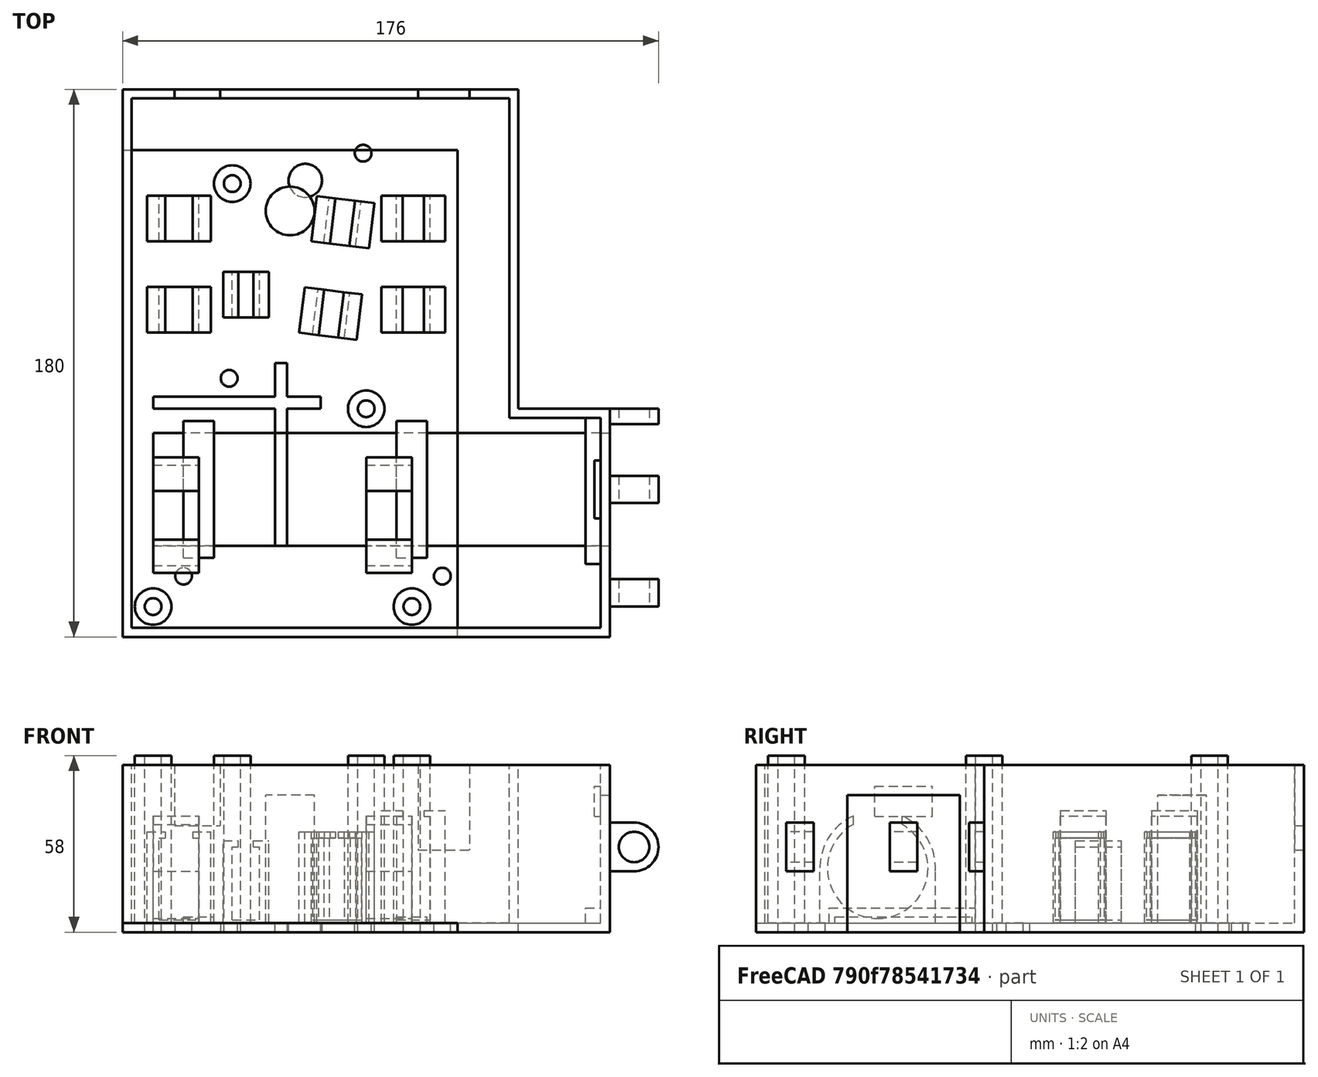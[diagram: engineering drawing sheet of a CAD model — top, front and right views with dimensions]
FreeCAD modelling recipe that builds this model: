
FCSTD DOCUMENT  (FreeCAD 0.16R6707 (Git))
Label: Akku_Peripherie
License: All rights reserved
LicenseURL: http://en.wikipedia.org/wiki/All_rights_reserved
objects: Part::Box×37, Part::Cylinder×23, Part::Cut×20, Part::MultiFuse×18, App::DocumentObjectGroup×4, Spreadsheet::Sheet×1, Mesh::Feature×1
note: 98 computed .brp shape members not serialized (recipe doc carries the construction recipe); baked Part::Feature solids carry a one-line shape summary decoded from their .brp

FEATURE [Part::Box] Box  label="Grundplatte"
  Height = 3
  Length = 110
  Width = 160
FEATURE [Part::Cylinder] Cylinder003  label="PowerCore"
  Angle = 360
  Height = 108
  Placement = pos=(0,40,21) rot=(0,1,0;1.5708rad)
  Radius = 16.5
FEATURE [Part::Cylinder] Cylinder004  label="PowerCore001"
  Angle = 360
  Height = 15
  Placement = pos=(10,40,21) rot=(0,1,0;1.5708rad)
  Radius = 19
FEATURE [Part::Cylinder] Cylinder005  label="PowerCore002"
  Angle = 360
  Height = 15
  Placement = pos=(80,40,21) rot=(0,1,0;1.5708rad)
  Radius = 19
FEATURE [Part::MultiFuse] Fusion
  Shapes = -> [Cylinder004,Cylinder005]
FEATURE [Part::Cut] Cut
  Base = -> Fusion
  Tool = -> Cylinder003
FEATURE [Part::Box] Box001  label="Würfel001"
  Height = 10
  Length = 108
  Placement = pos=(0,32,33) rot=(0,0,1;0rad)
  Width = 16
FEATURE [Part::Cut] Cut001  label="Anker Powerbank"
  Base = -> Cut
  Tool = -> Box001
FEATURE [Part::Cylinder] Cylinder  label="Hull Corner 1"
  Angle = 360
  Height = 55
  Placement = pos=(10,10,3) rot=(0,0,1;0rad)
  Radius = 6
FEATURE [Part::Cylinder] Cylinder006  label="Core Corner 4"
  Angle = 360
  Height = 70
  Placement = pos=(95,10,-3) rot=(0,0,1;0rad)
  Radius = 2.75
FEATURE [App::DocumentObjectGroup] Gruppe001  label="Devices"
FEATURE [Part::Box] Box002  label="DVB-T"
  Height = 27
  Length = 84
  Placement = pos=(25,80,4) rot=(0,0,1;1.5708rad)
  Width = 13
FEATURE [Part::Box] Box003  label="GPS"
  Height = 24
  Length = 52
  Placement = pos=(45,80,4) rot=(0,0,1;1.5708rad)
  Width = 9
FEATURE [Part::Cylinder] Cylinder007  label="Core Corner 2"
  Angle = 360
  Height = 70
  Placement = pos=(36,149,-3) rot=(0,0,1;0rad)
  Radius = 2.75
FEATURE [Part::Cylinder] Cylinder008  label="Hull Corner 2"
  Angle = 360
  Height = 55
  Placement = pos=(36,149,3) rot=(0,0,1;0rad)
  Radius = 6
FEATURE [Part::Cylinder] Cylinder009  label="Hull Corner 4"
  Angle = 360
  Height = 55
  Placement = pos=(95,10,3) rot=(0,0,1;0rad)
  Radius = 6
FEATURE [Part::Cylinder] Cylinder010  label="Core Corner 1"
  Angle = 360
  Height = 70
  Placement = pos=(10,10,-3) rot=(0,0,1;0rad)
  Radius = 2.75
FEATURE [Part::Box] Box004  label="Würfel002"
  Height = 33
  Length = 21
  Placement = pos=(8,100,0) rot=(0,0,1;0rad)
  Width = 15
FEATURE [Part::Box] Box005  label="Würfel003"
  Height = 33
  Length = 21
  Placement = pos=(8,130,0) rot=(0,0,1;0rad)
  Width = 15
FEATURE [Part::Box] Box006  label="Halterung"
  Height = 10
  Length = 9
  Placement = pos=(14,95,30) rot=(0,0,1;0rad)
  Width = 60
FEATURE [Part::MultiFuse] Fusion001
  Shapes = -> [Box005,Box004]
FEATURE [Part::Cut] Cut002
  Base = -> Fusion001
  Tool = -> Box006
FEATURE [Part::Cut] Cut003  label="DVB-T Halterung"
  Base = -> Cut002
  Tool = -> Box002
FEATURE [Part::Box] Box007  label="Würfel004"
  Height = 30
  Length = 15
  Placement = pos=(33,105,0) rot=(0,0,1;0rad)
  Width = 15
FEATURE [Part::Box] Box008  label="GPS001"
  Height = 24
  Length = 52
  Placement = pos=(43,80,10) rot=(0,0,1;1.5708rad)
  Width = 5
FEATURE [Part::MultiFuse] Fusion002
  Shapes = -> [Box008,Box003]
FEATURE [Part::Cut] Cut004  label="GPS Halterung"
  Base = -> Box007
  Tool = -> Fusion002
FEATURE [Part::Box] Box009  label="Würfel"
  Height = 55
  Length = 160
  Width = 180
FEATURE [Part::Box] Box010  label="Alfa"
  Height = 34
  Length = 11
  Placement = pos=(90,80,4) rot=(0,0,1;0rad)
  Width = 87
FEATURE [Part::Box] Box011  label="Würfel005"
  Height = 40
  Length = 21
  Placement = pos=(85,130,0) rot=(0,0,1;0rad)
  Width = 15
FEATURE [Part::Box] Box012  label="Würfel006"
  Height = 40
  Length = 21
  Placement = pos=(85,100,0) rot=(0,0,1;0rad)
  Width = 15
FEATURE [Part::MultiFuse] Fusion003
  Shapes = -> [Box012,Box011]
FEATURE [Part::Box] Box013  label="Alfa001"
  Height = 34
  Length = 7
  Placement = pos=(92,80,10) rot=(0,0,1;0rad)
  Width = 87
FEATURE [Part::MultiFuse] Fusion004
  Shapes = -> [Box013,Box010]
FEATURE [Part::Cut] Cut005  label="Alfa Halterung"
  Base = -> Fusion003
  Tool = -> Fusion004
FEATURE [Part::Cylinder] Cylinder012  label="Hull Corner 3"
  Angle = 360
  Height = 55
  Placement = pos=(80,75,3) rot=(0,0,1;0rad)
  Radius = 6
FEATURE [Part::Cylinder] Cylinder013  label="Core Corner 3"
  Angle = 360
  Height = 70
  Placement = pos=(80,75,-3) rot=(0,0,1;0rad)
  Radius = 2.75
FEATURE [Part::Box] Box014  label="Würfel007"
  Height = 55
  Length = 30
  Placement = pos=(130,75,0) rot=(0,0,1;0rad)
  Width = 105
FEATURE [Part::Box] Box015  label="Würfel008"
  Height = 55
  Length = 124
  Placement = pos=(3,3,3) rot=(0,0,1;0rad)
  Width = 174
FEATURE [Part::Box] Box016  label="Würfel009"
  Height = 55
  Length = 30
  Placement = pos=(127,3,3) rot=(0,0,1;0rad)
  Width = 69
FEATURE [Part::Cylinder] Cylinder014  label="Zylinder"
  Angle = 360
  Height = 10
  Placement = pos=(20,20,-3) rot=(0,0,1;0rad)
  Radius = 2.75
FEATURE [Part::Cylinder] Cylinder015  label="Zylinder001"
  Angle = 360
  Height = 10
  Placement = pos=(105,20,-3) rot=(0,0,1;0rad)
  Radius = 2.75
FEATURE [Part::Cylinder] Cylinder016  label="Zylinder002"
  Angle = 360
  Height = 10
  Placement = pos=(79,159,-3) rot=(0,0,1;0rad)
  Radius = 2.75
FEATURE [Part::Cylinder] Cylinder017  label="Zylinder003"
  Angle = 360
  Height = 10
  Placement = pos=(35,85,-3) rot=(0,0,1;0rad)
  Radius = 2.75
FEATURE [Part::Cylinder] Cylinder018  label="Zylinder004"
  Angle = 360
  Height = 10
  Placement = pos=(60,150,-3) rot=(0,0,1;0rad)
  Radius = 5.5
FEATURE [Part::MultiFuse] Fusion008
  Shapes = -> [Cylinder014,Cylinder015,Cylinder016,Cylinder017,Cylinder018]
FEATURE [Part::Box] Box017  label="Würfel010"
  Height = 28
  Length = 17
  Placement = pos=(97,170,27) rot=(0,0,1;0rad)
  Width = 20
FEATURE [Spreadsheet::Sheet] Spreadsheet
  cells = A1=Distanzhalter Höhe: 55 mm; B1=L; C1=B; D1=H; E1=X; F1=Y; G1=Z; A2=Bodenplatte; B2=110; C2=160; D2=3; E2=0; F2=0; G2=0; A3=Corner 1; B3=6; C3=6; D3=55; E3=10; F3=10; G3=3; A4=Corner 2; B4=6; C4=6; D4=55; E4=36; F4=149; G4=3; A5=Corner 3; B5=6; C5=6; D5=55; E5=80; F5=75; G5=3; A6=Corner 4; B6=6; C6=6; D6=55; E6=95; F6=10; G6=3; A7=DVB-T Antenne; B7=8; C7=8; D7=42; E7=55; F7=140; G7=3; A8=DVB-T Stick; B8=84; C8=13; D8=27; E8=25; F8=80; G8=4; A9=GPS Stick; B9=52; C9=9; D9=24; E9=45; F9=80; G9=4; A10=Alfa Stick; B10=11; C10=87; D10=34; E10=90; F10=80; G10=4; A12=Deckel; B12=180; C12=160; D12=55; E12=0; F12=0; G12=0; A13=Cutoff; B13=105; C13=30; D13=55; E13=130; F13=75; G13=0; A14=Auslass DVB-T; B14=17; C14=20; D14=28; E14==130 - 10 - 25 + 2; F14=170; G14=27; A15=Auslass Alfa; B15=15; C15=20; D15=20; E15==130 - 10 - 90 - 13; F15=170; G15=35; A16=Akkuauslass; B16=150; C16=37; D16=45; E16=10; F16=30; G16=0; A18=HUAWEI Stick; B18=81; C18=10.5; D18=27
FEATURE [Part::MultiFuse] Fusion009
  Shapes = -> [Box,Cylinder,Cylinder008,Cylinder009,Cylinder012]
FEATURE [Part::MultiFuse] Fusion010
  Shapes = -> [Cylinder006,Cylinder007,Cylinder010,Cylinder013]
FEATURE [Part::Cut] Cut011  label="Bodenplatte ganz"
  Base = -> Fusion009
  Tool = -> Fusion010
FEATURE [Part::Cylinder] Cylinder011  label="DVB-T Antenne"
  Angle = 360
  Height = 42
  Placement = pos=(55,140,3) rot=(0,0,1;0rad)
  Radius = 8
FEATURE [Part::Cut] Cut012
  Base = -> Box009
  Tool = -> Box014
FEATURE [Part::MultiFuse] Fusion011
  Shapes = -> [Box015,Box016]
FEATURE [Part::Cut] Cut013
  Base = -> Cut012
  Tool = -> Fusion011
FEATURE [Part::Cut] Cut014
  Base = -> Cut013
  Tool = -> Fusion008
FEATURE [Part::Box] Box018  label="Würfel011"
  Height = 20
  Length = 15
  Placement = pos=(17,170,35) rot=(0,0,1;0rad)
  Width = 20
FEATURE [Part::MultiFuse] Fusion012
  Shapes = -> [Box017,Box018]
FEATURE [Part::Cut] Cut015
  Base = -> Cut014
  Tool = -> Fusion012
FEATURE [Part::Box] Box019  label="Würfel012"
  Height = 10
  Length = 55
  Placement = pos=(10,75,-3) rot=(0,0,1;0rad)
  Width = 4
FEATURE [Part::Box] Box020  label="Würfel013"
  Height = 10
  Length = 4
  Placement = pos=(50,30,-3) rot=(0,0,1;0rad)
  Width = 60
FEATURE [Part::MultiFuse] Fusion013
  Shapes = -> [Box019,Box020]
FEATURE [Part::Cut] Cut016  label="Bodenplatte"
  Base = -> Cut011
  Tool = -> Fusion013
FEATURE [Part::Box] Box021  label="Würfel014"
  Height = 45
  Length = 150
  Placement = pos=(10,30,0) rot=(0,0,1;0rad)
  Width = 37
FEATURE [Part::Box] Box022  label="Würfel015"
  Height = 5
  Length = 5
  Placement = pos=(152,24,3) rot=(0,0,1;0rad)
  Width = 48
FEATURE [Part::Cut] Cut017
  Base = -> Cut015
  Tool = -> Box021
FEATURE [Part::Box] Box023  label="Würfel016"
  Height = 45
  Length = 150
  Width = 37
FEATURE [Part::Box] Box024  label="Würfel017"
  Height = 45
  Length = 150
  Placement = pos=(-3,0,3) rot=(0,0,1;0rad)
  Width = 37
FEATURE [Part::Cut] Cut018
  Base = -> Box023
  Placement = pos=(10,30,0) rot=(0,0,1;0rad)
  Tool = -> Box024
FEATURE [Part::Box] Box025  label="Würfel018"
  Height = 2
  Length = 10
  Placement = pos=(20,26,3) rot=(0,0,1;0rad)
  Width = 45
FEATURE [Part::Box] Box026  label="Würfel019"
  Height = 2
  Length = 10
  Placement = pos=(90,26,3) rot=(0,0,1;0rad)
  Width = 45
FEATURE [Part::Box] Box027  label="Würfel020"
  Height = 10
  Length = 2
  Placement = pos=(155,39,38) rot=(0,0,1;0rad)
  Width = 19
FEATURE [Part::Cylinder] Cylinder019  label="Zylinder005"
  Angle = 360
  Height = 9
  Placement = pos=(8,9,8) rot=(1,0,0;1.5708rad)
  Radius = 8
FEATURE [Part::Box] Box029  label="Würfel022"
  Height = 16
  Length = 8
  Width = 9
FEATURE [Part::Cylinder] Cylinder020  label="Zylinder006"
  Angle = 360
  Height = 9
  Placement = pos=(8,9,8) rot=(1,0,0;1.5708rad)
  Radius = 5
FEATURE [Part::MultiFuse] Fusion014
  Shapes = -> [Cylinder019,Box029]
FEATURE [Part::Cut] Cut019  label="Fixieröse"
  Base = -> Fusion014
  Placement = pos=(160,44,20) rot=(0,0,1;0rad)
  Tool = -> Cylinder020
FEATURE [App::DocumentObjectGroup] Gruppe  label="Akkuauslass"
  Group = -> [Cut018,Box025,Box026,Box027,Cut019]
FEATURE [Part::Cylinder] Cylinder021  label="Zylinder007"
  Angle = 360
  Height = 9
  Placement = pos=(8,9,8) rot=(1,0,0;1.5708rad)
  Radius = 8
FEATURE [Part::Box] Box030  label="Würfel023"
  Height = 16
  Length = 8
  Width = 9
FEATURE [Part::Cylinder] Cylinder022  label="Zylinder008"
  Angle = 360
  Height = 9
  Placement = pos=(8,9,8) rot=(1,0,0;1.5708rad)
  Radius = 5
FEATURE [Part::MultiFuse] Fusion015
  Shapes = -> [Cylinder021,Box030]
FEATURE [Part::Cut] Cut020  label="Fixieröse001"
  Base = -> Fusion015
  Placement = pos=(160,10,20) rot=(0,0,1;0rad)
  Tool = -> Cylinder022
FEATURE [Part::Cylinder] Cylinder023  label="Zylinder009"
  Angle = 360
  Height = 5
  Placement = pos=(8,5,8) rot=(1,0,0;1.5708rad)
  Radius = 8
FEATURE [Part::Box] Box031  label="Würfel024"
  Height = 16
  Length = 8
  Width = 5
FEATURE [Part::Cylinder] Cylinder024  label="Zylinder010"
  Angle = 360
  Height = 5
  Placement = pos=(8,5,8) rot=(1,0,0;1.5708rad)
  Radius = 5
FEATURE [Part::MultiFuse] Fusion016
  Shapes = -> [Cylinder023,Box031]
FEATURE [Part::Cut] Cut021  label="Fixieröse schmal"
  Base = -> Fusion016
  Placement = pos=(160,70,20) rot=(0,0,1;0rad)
  Tool = -> Cylinder024
FEATURE [App::DocumentObjectGroup] Gruppe003  label="Deckel"
  Group = -> [Box022,Cut017,Cut020,Cut021]
FEATURE [Part::Box] Box032  label="Würfel025"
  Height = 19
  Length = 15
  Placement = pos=(10,21,1) rot=(0,0,1;0rad)
  Width = 38
FEATURE [Part::Box] Box033  label="Würfel026"
  Height = 19
  Length = 15
  Placement = pos=(80,21,1) rot=(0,0,1;0rad)
  Width = 38
FEATURE [Part::Cut] Cut022
  Base = -> Box032
  Tool = -> Cylinder004
FEATURE [Part::Cut] Cut023
  Base = -> Box033
  Tool = -> Cylinder005
FEATURE [Part::MultiFuse] Fusion017  label="Anker Powerbank stabil"
  Shapes = -> [Cut022,Cut023,Cut001]
FEATURE [Part::Box] Box034  label="Huawei"
  Height = 27
  Length = 10.5
  Placement = pos=(60,80,4) rot=(0,0,-1;0.122173rad)
  Width = 81
FEATURE [Part::Box] Box035  label="Huawei Cutoff"
  Height = 34
  Length = 6.5
  Placement = pos=(62,80,10) rot=(0,0,-1;0.122173rad)
  Width = 81
FEATURE [Part::Box] Box036  label="Würfel027"
  Height = 33
  Length = 19
  Placement = pos=(58,100,0) rot=(0,0,-1;0.122173rad)
  Width = 15
FEATURE [Part::Box] Box037  label="Würfel028"
  Height = 33
  Length = 19
  Placement = pos=(62,130,0) rot=(0,0,-1;0.122173rad)
  Width = 15
FEATURE [Part::MultiFuse] Fusion018
  Shapes = -> [Box036,Box037]
FEATURE [Part::MultiFuse] Fusion019
  Shapes = -> [Box035,Box034]
FEATURE [Part::Cut] Cut024  label="HUAWEI Halterung"
  Base = -> Fusion018
  Tool = -> Fusion019
FEATURE [Part::MultiFuse] Fusion020
  Shapes = -> [Cylinder011,Cut004,Cut003,Cut024,Cut005,Cut016,Fusion017]
FEATURE [App::DocumentObjectGroup] Gruppe004  label="Boden"
  Group = -> [Gruppe001,Fusion020]
FEATURE [Mesh::Feature] Mesh  label="Fusion020 (Meshed)"
